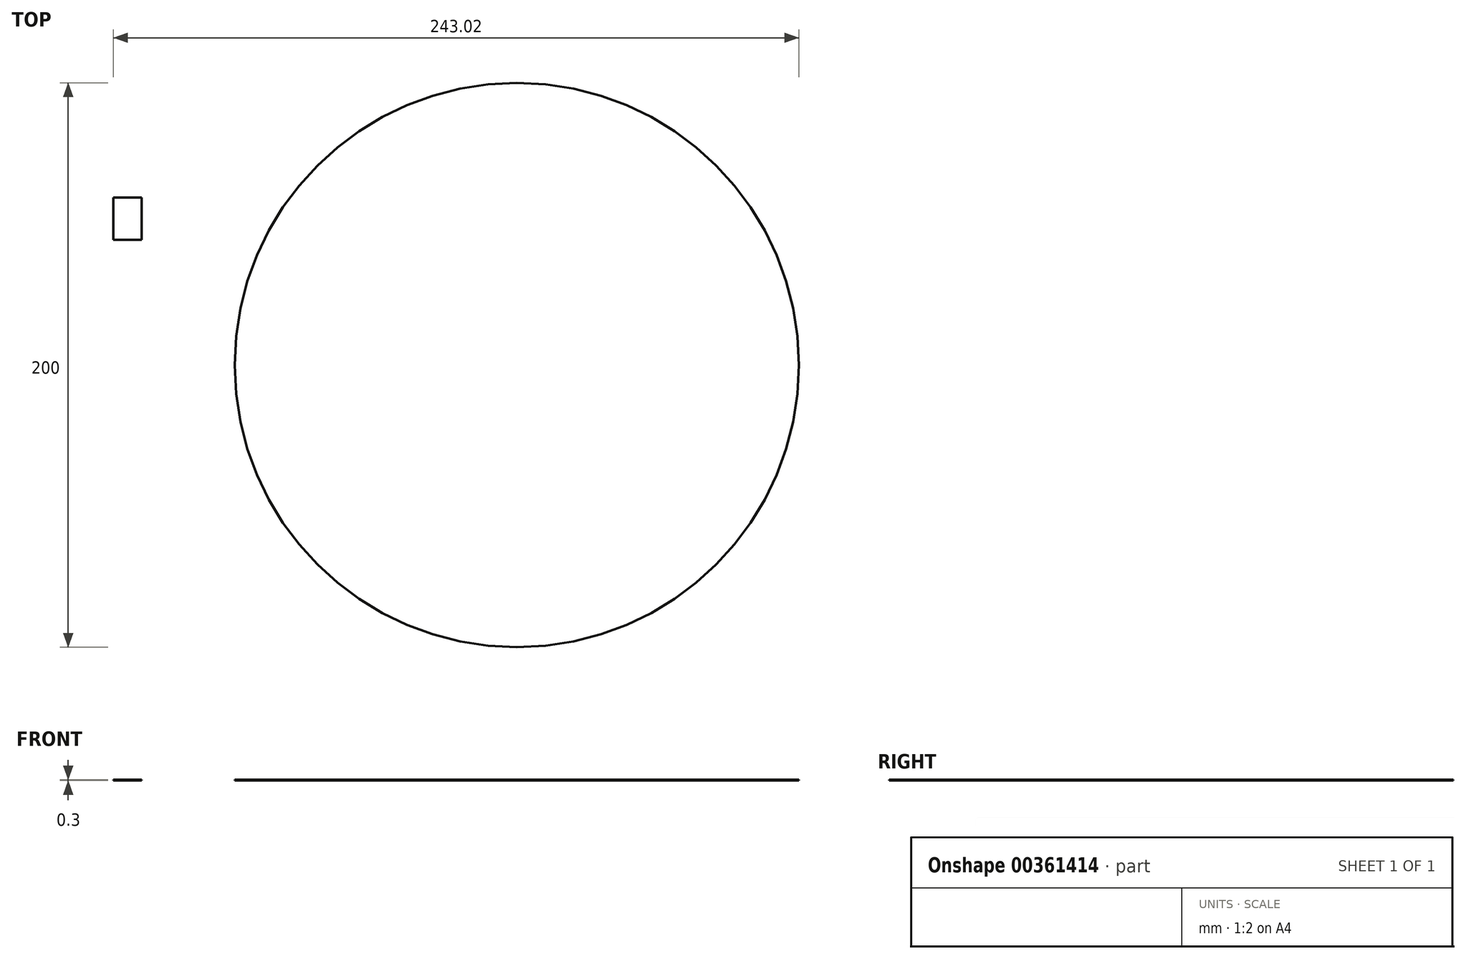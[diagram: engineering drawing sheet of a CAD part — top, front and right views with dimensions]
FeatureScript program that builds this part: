
annotation { "Feature Type Name" : "Feature", "Feature Type Description" : "" }
export const myFeature = defineFeature(function(context is Context, id is Id, definition is map)
    precondition{}
    {
        {
            var Q0;
            Q0=qCreatedBy(makeId("Top.planeOp"),FACE);
            var sketch = newSketch(context, id + "F0", { "sketchPlane" : qUnion([Q0])});
            skCircle(sketch, "E0", {"center": v(0, 0) * mm, "radius": 100 * mm});
            skLineSegment(sketch, "E1.bottom", {"start": v(-143.02, 59.33) * mm, "end": v(-133.02, 59.33) * mm});
            skLineSegment(sketch, "E1.top", {"start": v(-143.02, 44.33) * mm, "end": v(-133.02, 44.33) * mm});
            skLineSegment(sketch, "E1.left", {"start": v(-143.02, 59.33) * mm, "end": v(-143.02, 44.33) * mm});
            skLineSegment(sketch, "E1.right", {"start": v(-133.02, 59.33) * mm, "end": v(-133.02, 44.33) * mm});
            skSolve(sketch);
        }
        {
            var Q0;
            Q0=makeQuery(id+"F0.imprint","IMPRINT",FACE,{"disambiguationData":[TD([[makeQuery(id+"F0.imprint","IMPRINT",EDGE,{"derivedFrom":sQuery(id+"F0.wireOp",EDGE,"E0")}),1.0]])]});
            var Q1;
            Q1=makeQuery(id+"F0.imprint","IMPRINT",FACE,{"disambiguationData":[TD([[makeQuery(id+"F0.imprint","IMPRINT",EDGE,{"derivedFrom":sQuery(id+"F0.wireOp",EDGE,"E1.bottom")}),-1.0]])]});
            extrude(context, id + "F1", {"entities" : qUnion([Q0, Q1]), "depth" : 0.3 * mm});
        }
    });
